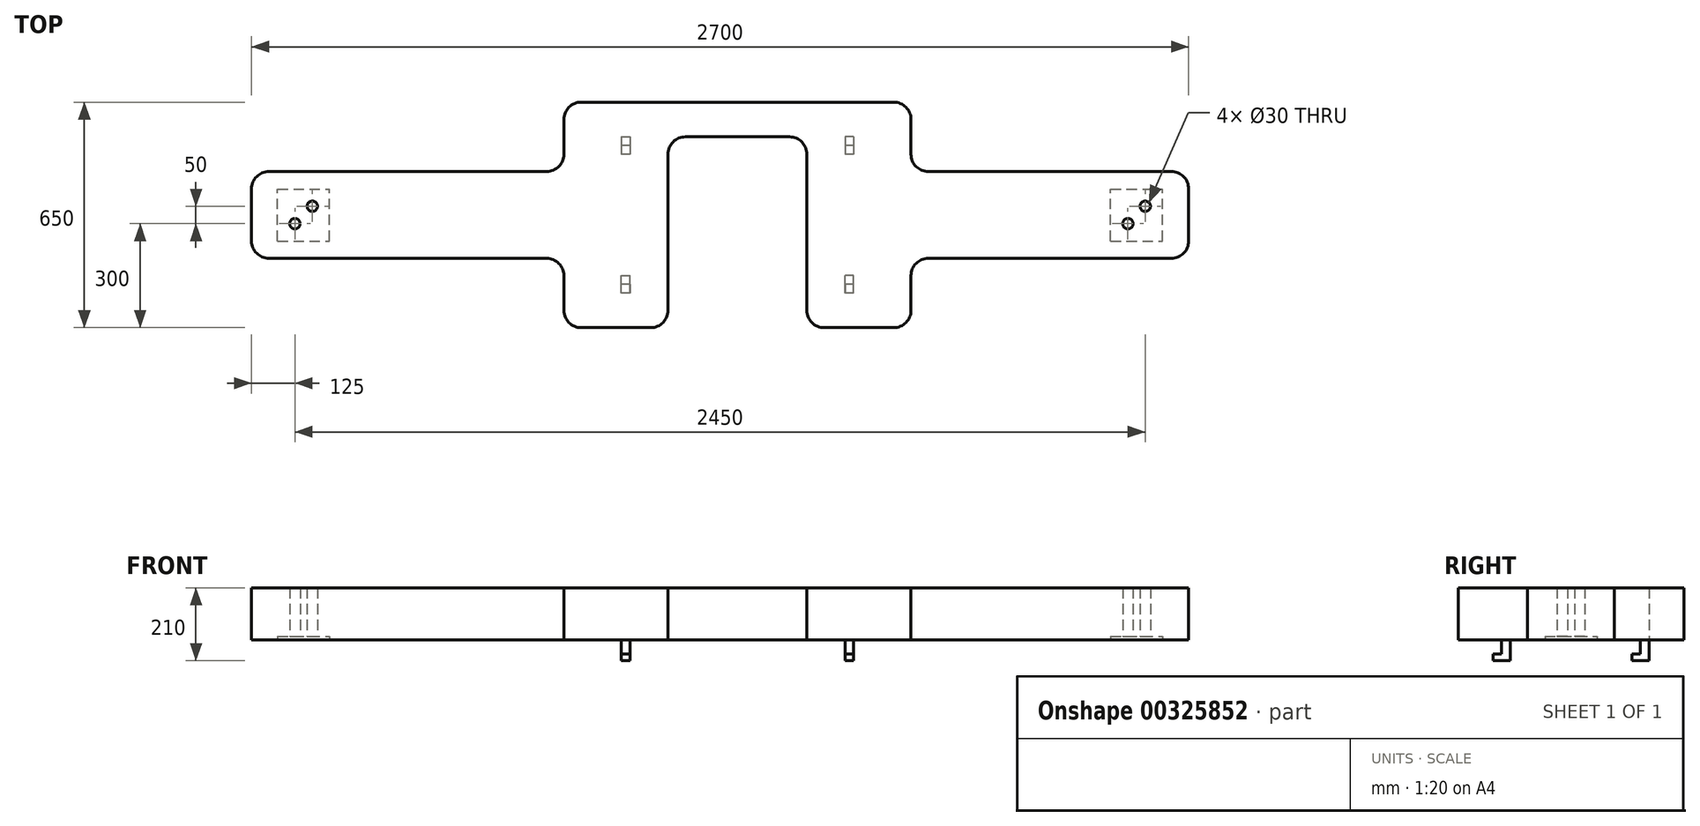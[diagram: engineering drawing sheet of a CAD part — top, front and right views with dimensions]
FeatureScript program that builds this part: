
annotation { "Feature Type Name" : "Feature", "Feature Type Description" : "" }
export const myFeature = defineFeature(function(context is Context, id is Id, definition is map)
    precondition{}
    {
        {
            var Q0;
            Q0=qCreatedBy(makeId("Top.planeOp"),FACE);
            var sketch = newSketch(context, id + "F0", { "sketchPlane" : qUnion([Q0])});
            skLineSegment(sketch, "E0", {"start": v(0, 0) * mm, "end": v(0, 250) * mm});
            skLineSegment(sketch, "E1", {"start": v(0, 250) * mm, "end": v(900, 250) * mm});
            skLineSegment(sketch, "E2.left", {"start": v(2700, 0) * mm, "end": v(2700, 250) * mm});
            skLineSegment(sketch, "E3", {"start": v(900, 250) * mm, "end": v(900, 450) * mm});
            skLineSegment(sketch, "E4", {"start": v(900, 450) * mm, "end": v(1900, 450) * mm});
            skLineSegment(sketch, "E5", {"start": v(1900, 450) * mm, "end": v(1900, 250) * mm});
            skLineSegment(sketch, "E6", {"start": v(1900, 0) * mm, "end": v(1900, -200) * mm});
            skLineSegment(sketch, "E7", {"start": v(1900, -200) * mm, "end": v(1600, -200) * mm});
            skLineSegment(sketch, "E8", {"start": v(1600, -200) * mm, "end": v(1600, 350) * mm});
            skLineSegment(sketch, "E9", {"start": v(1200, 350) * mm, "end": v(1600, 350) * mm});
            skLineSegment(sketch, "E10", {"start": v(2700, 250) * mm, "end": v(1900, 250) * mm});
            skLineSegment(sketch, "E11", {"start": v(2700, 0) * mm, "end": v(1900, 0) * mm});
            skLineSegment(sketch, "E12", {"start": v(0, 0) * mm, "end": v(900, 0) * mm});
            skLineSegment(sketch, "E13", {"start": v(900, 0) * mm, "end": v(900, -200) * mm});
            skLineSegment(sketch, "E14", {"start": v(900, -200) * mm, "end": v(1200, -200) * mm});
            skLineSegment(sketch, "E15", {"start": v(1200, -200) * mm, "end": v(1200, 350) * mm});
            skLineSegment(sketch, "E16", {"start": v(0, 125) * mm, "end": v(2700, 125) * mm, "construction": true});
            skSolve(sketch);
        }
        {
            var Q0;
            Q0 = qSketchRegion(id + "F0", true);
            extrude(context, id + "F1", {"entities" : qUnion([Q0]), "depth" : 150 * mm});
        }
        {
            var Q0;
            Q0=makeQuery(id+"F1.opExtrude","SWEPT_EDGE",EDGE,{"disambiguationData":[OSD([sQuery(id+"F0.wireOp",EDGE,"E8"),sQuery(id+"F0.wireOp",EDGE,"E9")])]});
            var Q1;
            Q1=makeQuery(id+"F1.opExtrude","SWEPT_EDGE",EDGE,{"disambiguationData":[OSD([sQuery(id+"F0.wireOp",EDGE,"CbPWlrPQ-xpmH-DLCr-Jztd-sM4HRHclp71n"),sQuery(id+"F0.wireOp",EDGE,"E9")])]});
            var Q2;
            Q2=makeQuery(id+"F1.opExtrude","SWEPT_EDGE",EDGE,{"disambiguationData":[OSD([sQuery(id+"F0.wireOp",EDGE,"VvWYzF3Y-HK12-tJQy-JKRe-ZAa0soEaOskw"),sQuery(id+"F0.wireOp",EDGE,"CbPWlrPQ-xpmH-DLCr-Jztd-sM4HRHclp71n")])]});
            var Q3;
            Q3=makeQuery(id+"F1.opExtrude","SWEPT_EDGE",EDGE,{"disambiguationData":[OSD([sQuery(id+"F0.wireOp",EDGE,"2RDTeN5u-19Zg-kb8m-eJnc-UEhqzuxQh641"),sQuery(id+"F0.wireOp",EDGE,"VvWYzF3Y-HK12-tJQy-JKRe-ZAa0soEaOskw")])]});
            var Q4;
            Q4=makeQuery(id+"F1.opExtrude","SWEPT_EDGE",EDGE,{"disambiguationData":[OSD([sQuery(id+"F0.wireOp",EDGE,"E7"),sQuery(id+"F0.wireOp",EDGE,"E8")])]});
            var Q5;
            Q5=makeQuery(id+"F1.opExtrude","SWEPT_EDGE",EDGE,{"disambiguationData":[OSD([sQuery(id+"F0.wireOp",EDGE,"E6"),sQuery(id+"F0.wireOp",EDGE,"E7")])]});
            var Q6;
            Q6=makeQuery(id+"F1.opExtrude","SWEPT_EDGE",EDGE,{"disambiguationData":[OSD([sQuery(id+"F0.wireOp",EDGE,"E2.bottom"),sQuery(id+"F0.wireOp",EDGE,"E6")])]});
            var Q7;
            Q7=makeQuery(id+"F1.opExtrude","SWEPT_EDGE",EDGE,{"disambiguationData":[OSD([sQuery(id+"F0.wireOp",EDGE,"E2.top"),sQuery(id+"F0.wireOp",EDGE,"E5")])]});
            var Q8;
            Q8=makeQuery(id+"F1.opExtrude","SWEPT_EDGE",EDGE,{"disambiguationData":[OSD([sQuery(id+"F0.wireOp",EDGE,"E4"),sQuery(id+"F0.wireOp",EDGE,"E5")])]});
            var Q9;
            Q9=makeQuery(id+"F1.opExtrude","SWEPT_EDGE",EDGE,{"disambiguationData":[OSD([sQuery(id+"F0.wireOp",EDGE,"E2.top"),sQuery(id+"F0.wireOp",EDGE,"E2.left")])]});
            var Q10;
            Q10=makeQuery(id+"F1.opExtrude","SWEPT_EDGE",EDGE,{"disambiguationData":[OSD([sQuery(id+"F0.wireOp",EDGE,"E2.bottom"),sQuery(id+"F0.wireOp",EDGE,"E2.left")])]});
            var Q11;
            Q11=makeQuery(id+"F1.opExtrude","SWEPT_EDGE",EDGE,{"disambiguationData":[OSD([sQuery(id+"F0.wireOp",EDGE,"E3"),sQuery(id+"F0.wireOp",EDGE,"E4")])]});
            var Q12;
            Q12=makeQuery(id+"F1.opExtrude","SWEPT_EDGE",EDGE,{"disambiguationData":[OSD([sQuery(id+"F0.wireOp",EDGE,"E1"),sQuery(id+"F0.wireOp",EDGE,"E3")])]});
            var Q13;
            Q13=makeQuery(id+"F1.opExtrude","SWEPT_EDGE",EDGE,{"disambiguationData":[OSD([sQuery(id+"F0.wireOp",EDGE,"E0"),sQuery(id+"F0.wireOp",EDGE,"E1")])]});
            var Q14;
            Q14=makeQuery(id+"F1.opExtrude","SWEPT_EDGE",EDGE,{"disambiguationData":[OSD([sQuery(id+"F0.wireOp",EDGE,"E0"),sQuery(id+"F0.wireOp",EDGE,"RZtDIs5I-CLOF-AWdb-lgDT-qq9BP0aAqrrl")])]});
            var Q15;
            Q15=makeQuery(id+"F1.opExtrude","SWEPT_EDGE",EDGE,{"disambiguationData":[OSD([sQuery(id+"F0.wireOp",EDGE,"RZtDIs5I-CLOF-AWdb-lgDT-qq9BP0aAqrrl"),sQuery(id+"F0.wireOp",EDGE,"2RDTeN5u-19Zg-kb8m-eJnc-UEhqzuxQh641")])]});
            fillet(context, id + "F2", {"entities" : qUnion([Q0, Q1, Q2, Q3, Q4, Q5, Q6, Q7, Q8, Q9, Q10, Q11, Q12, Q13, Q14, Q15]), "radius" : 50 * mm, "tangentPropagation" : true, "allowEdgeOverflow" : false});
        }
        {
            var Q0;
            Q0=makeQuery(id+"F1.opExtrude","CAP_FACE",FACE,{"disambiguationData":[OSD([sQuery(id+"F0.wireOp",EDGE,"E0"),sQuery(id+"F0.wireOp",EDGE,"E1"),sQuery(id+"F0.wireOp",EDGE,"RZtDIs5I-CLOF-AWdb-lgDT-qq9BP0aAqrrl"),sQuery(id+"F0.wireOp",EDGE,"E2.bottom"),sQuery(id+"F0.wireOp",EDGE,"E2.top"),sQuery(id+"F0.wireOp",EDGE,"E2.left"),sQuery(id+"F0.wireOp",EDGE,"E3"),sQuery(id+"F0.wireOp",EDGE,"E4"),sQuery(id+"F0.wireOp",EDGE,"E5"),sQuery(id+"F0.wireOp",EDGE,"E6"),sQuery(id+"F0.wireOp",EDGE,"E7"),sQuery(id+"F0.wireOp",EDGE,"E8"),sQuery(id+"F0.wireOp",EDGE,"2RDTeN5u-19Zg-kb8m-eJnc-UEhqzuxQh641"),sQuery(id+"F0.wireOp",EDGE,"VvWYzF3Y-HK12-tJQy-JKRe-ZAa0soEaOskw"),sQuery(id+"F0.wireOp",EDGE,"CbPWlrPQ-xpmH-DLCr-Jztd-sM4HRHclp71n"),sQuery(id+"F0.wireOp",EDGE,"E9")])],"isStart":true});
            var sketch = newSketch(context, id + "F3", { "sketchPlane" : qUnion([Q0])});
            skLineSegment(sketch, "E17.bottom", {"start": v(75, -50) * mm, "end": v(225, -50) * mm});
            skLineSegment(sketch, "E17.top", {"start": v(75, -200) * mm, "end": v(225, -200) * mm});
            skLineSegment(sketch, "E17.left", {"start": v(75, -50) * mm, "end": v(75, -200) * mm});
            skLineSegment(sketch, "E17.right", {"start": v(225, -50) * mm, "end": v(225, -200) * mm});
            skLineSegment(sketch, "E18.bottom", {"start": v(2475, -50) * mm, "end": v(2625, -50) * mm});
            skLineSegment(sketch, "E18.top", {"start": v(2475, -200) * mm, "end": v(2625, -200) * mm});
            skLineSegment(sketch, "E18.left", {"start": v(2475, -50) * mm, "end": v(2475, -200) * mm});
            skLineSegment(sketch, "E18.right", {"start": v(2625, -50) * mm, "end": v(2625, -200) * mm});
            skLineSegment(sketch, "E19", {"start": v(120, 0) * mm, "end": v(120, -50) * mm, "construction": true});
            skLineSegment(sketch, "E20", {"start": v(0, -125) * mm, "end": v(75, -125) * mm, "construction": true});
            skPoint(sketch, "E20.endSnap0", {"position": v(75, -125) * mm});
            skLineSegment(sketch, "E21", {"start": v(2625, -125) * mm, "end": v(2700, -125) * mm, "construction": true});
            skSolve(sketch);
        }
        {
            var Q0;
            Q0=makeQuery(id+"F3.imprint","IMPRINT",FACE,{"disambiguationData":[TD([[makeQuery(id+"F3.imprint","IMPRINT",EDGE,{"derivedFrom":sQuery(id+"F3.wireOp",EDGE,"E17.bottom")}),-1.0]])]});
            var Q1;
            Q1=makeQuery(id+"F3.imprint","IMPRINT",FACE,{"disambiguationData":[TD([[makeQuery(id+"F3.imprint","IMPRINT",EDGE,{"derivedFrom":sQuery(id+"F3.wireOp",EDGE,"E18.bottom")}),-1.0]])]});
            extrude(context, id + "F4", {"entities" : qUnion([Q0, Q1]), "operationType" : NewBodyOperationType.REMOVE, "oppositeDirection" : true, "depth" : 10 * mm});
        }
        {
            var Q0;
            Q0=makeQuery(id+"F1.opExtrude","SWEPT_EDGE",EDGE,{"disambiguationData":[OSD([sQuery(id+"F0.wireOp",EDGE,"E14"),sQuery(id+"F0.wireOp",EDGE,"E15")])]});
            var Q1;
            Q1=makeQuery(id+"F1.opExtrude","SWEPT_EDGE",EDGE,{"disambiguationData":[OSD([sQuery(id+"F0.wireOp",EDGE,"E13"),sQuery(id+"F0.wireOp",EDGE,"E14")])]});
            var Q2;
            Q2=makeQuery(id+"F1.opExtrude","SWEPT_EDGE",EDGE,{"disambiguationData":[OSD([sQuery(id+"F0.wireOp",EDGE,"E12"),sQuery(id+"F0.wireOp",EDGE,"E13")])]});
            fillet(context, id + "F5", {"entities" : qUnion([Q0, Q1, Q2]), "radius" : 50 * mm, "tangentPropagation" : true, "allowEdgeOverflow" : false});
        }
        {
            var Q0;
            Q0=makeQuery(id+"F4.boolean.opBoolean","COPY",FACE,{"derivedFrom":makeQuery(id+"F4.opExtrude","CAP_FACE",FACE,{"disambiguationData":[OSD([sQuery(id+"F3.wireOp",EDGE,"E17.bottom"),sQuery(id+"F3.wireOp",EDGE,"E17.top"),sQuery(id+"F3.wireOp",EDGE,"E17.left"),sQuery(id+"F3.wireOp",EDGE,"E17.right")])],"isStart":false})});
            var sketch = newSketch(context, id + "F6", { "sketchPlane" : qUnion([Q0])});
            skCircle(sketch, "E22", {"center": v(125, -100) * mm, "radius": 15 * mm});
            skCircle(sketch, "E23", {"center": v(175, -150) * mm, "radius": 15 * mm});
            skLineSegment(sketch, "E24", {"start": v(125, -100) * mm, "end": v(125, -50) * mm, "construction": true});
            skLineSegment(sketch, "E25", {"start": v(175, -150) * mm, "end": v(175, -200) * mm, "construction": true});
            skSolve(sketch);
        }
        {
            var Q0;
            Q0=makeQuery(id+"F6.imprint","IMPRINT",FACE,{"disambiguationData":[TD([[makeQuery(id+"F6.imprint","IMPRINT",EDGE,{"derivedFrom":sQuery(id+"F6.wireOp",EDGE,"E23")}),1.0]])]});
            var Q1;
            Q1=makeQuery(id+"F6.imprint","IMPRINT",FACE,{"disambiguationData":[TD([[makeQuery(id+"F6.imprint","IMPRINT",EDGE,{"derivedFrom":sQuery(id+"F6.wireOp",EDGE,"E22")}),1.0]])]});
            var Q2;
            Q2=sQuery(id+"F6.wireOp",EDGE,"E22");
            var Q3;
            Q3=sQuery(id+"F6.wireOp",EDGE,"E23");
            extrude(context, id + "F7", {"entities" : qUnion([Q0, Q1]), "operationType" : NewBodyOperationType.REMOVE, "surfaceEntities" : qUnion([Q2, Q3]), "oppositeDirection" : true, "depth" : 200 * mm});
        }
        {
            var Q0;
            Q0=makeQuery(id+"F4.boolean.opBoolean","COPY",FACE,{"derivedFrom":makeQuery(id+"F4.opExtrude","CAP_FACE",FACE,{"disambiguationData":[OSD([sQuery(id+"F3.wireOp",EDGE,"E18.bottom"),sQuery(id+"F3.wireOp",EDGE,"E18.top"),sQuery(id+"F3.wireOp",EDGE,"E18.left"),sQuery(id+"F3.wireOp",EDGE,"E18.right")])],"isStart":false})});
            var sketch = newSketch(context, id + "F8", { "sketchPlane" : qUnion([Q0])});
            skCircle(sketch, "E26", {"center": v(2525, -100) * mm, "radius": 15 * mm});
            skCircle(sketch, "E27", {"center": v(2575, -150) * mm, "radius": 15 * mm});
            skLineSegment(sketch, "E28", {"start": v(2525, -100) * mm, "end": v(2475, -100) * mm, "construction": true});
            skLineSegment(sketch, "E29", {"start": v(2575, -150) * mm, "end": v(2625, -150) * mm, "construction": true});
            skLineSegment(sketch, "E30", {"start": v(2525, -100) * mm, "end": v(2525, -50) * mm, "construction": true});
            skLineSegment(sketch, "E31", {"start": v(2575, -150) * mm, "end": v(2575, -200) * mm, "construction": true});
            skSolve(sketch);
        }
        {
            var Q0;
            Q0 = qSketchRegion(id + "F8", true);
            extrude(context, id + "F9", {"entities" : qUnion([Q0]), "operationType" : NewBodyOperationType.REMOVE, "oppositeDirection" : true, "depth" : 200 * mm});
        }
        {
            var Q0;
            Q0=makeQuery(id+"F1.opExtrude","CAP_FACE",FACE,{"disambiguationData":[OSD([sQuery(id+"F0.wireOp",EDGE,"E0"),sQuery(id+"F0.wireOp",EDGE,"E1"),sQuery(id+"F0.wireOp",EDGE,"E2.left"),sQuery(id+"F0.wireOp",EDGE,"E3"),sQuery(id+"F0.wireOp",EDGE,"E4"),sQuery(id+"F0.wireOp",EDGE,"E5"),sQuery(id+"F0.wireOp",EDGE,"E6"),sQuery(id+"F0.wireOp",EDGE,"E7"),sQuery(id+"F0.wireOp",EDGE,"E8"),sQuery(id+"F0.wireOp",EDGE,"E9"),sQuery(id+"F0.wireOp",EDGE,"E10"),sQuery(id+"F0.wireOp",EDGE,"E11"),sQuery(id+"F0.wireOp",EDGE,"E12"),sQuery(id+"F0.wireOp",EDGE,"E13"),sQuery(id+"F0.wireOp",EDGE,"E14"),sQuery(id+"F0.wireOp",EDGE,"E15")])],"isStart":true});
            var sketch = newSketch(context, id + "F10", { "sketchPlane" : qUnion([Q0])});
            skLineSegment(sketch, "E32.bottom", {"start": v(1065, 100) * mm, "end": v(1090, 100) * mm});
            skLineSegment(sketch, "E32.top", {"start": v(1065, 50) * mm, "end": v(1090, 50) * mm});
            skLineSegment(sketch, "E32.left", {"start": v(1065, 100) * mm, "end": v(1065, 50) * mm});
            skLineSegment(sketch, "E32.right", {"start": v(1090, 100) * mm, "end": v(1090, 50) * mm});
            skLineSegment(sketch, "E33.MirrorCS", {"start": v(1735, 100) * mm, "end": v(1710, 100) * mm});
            skLineSegment(sketch, "E34.MirrorCS", {"start": v(1735, 50) * mm, "end": v(1710, 50) * mm});
            skLineSegment(sketch, "E35.MirrorCS", {"start": v(1710, 100) * mm, "end": v(1710, 50) * mm});
            skLineSegment(sketch, "E36.MirrorCS", {"start": v(1735, 100) * mm, "end": v(1735, 50) * mm});
            skLineSegment(sketch, "E37.MirrorCS", {"start": v(1065, -300) * mm, "end": v(1090, -300) * mm});
            skLineSegment(sketch, "E38.MirrorCS", {"start": v(1065, -350) * mm, "end": v(1090, -350) * mm});
            skLineSegment(sketch, "E39.MirrorCS", {"start": v(1735, -300) * mm, "end": v(1710, -300) * mm});
            skLineSegment(sketch, "E40.MirrorCS", {"start": v(1735, -350) * mm, "end": v(1710, -350) * mm});
            skLineSegment(sketch, "E41.MirrorCS", {"start": v(1065, -350) * mm, "end": v(1065, -300) * mm});
            skLineSegment(sketch, "E42.MirrorCS", {"start": v(1735, -350) * mm, "end": v(1735, -300) * mm});
            skLineSegment(sketch, "E43.MirrorCS", {"start": v(1710, -350) * mm, "end": v(1710, -300) * mm});
            skLineSegment(sketch, "E44.MirrorCS", {"start": v(1090, -350) * mm, "end": v(1090, -300) * mm});
            skSolve(sketch);
        }
        {
            var Q0;
            Q0 = qSketchRegion(id + "F10", true);
            extrude(context, id + "F11", {"entities" : qUnion([Q0]), "operationType" : NewBodyOperationType.ADD, "depth" : 60 * mm});
        }
        {
            var Q0;
            Q0=makeQuery(id+"F11.opExtrude","SWEPT_FACE",FACE,{"disambiguationData":[OSD([sQuery(id+"F10.wireOp",EDGE,"E32.left")])]});
            var sketch = newSketch(context, id + "F12", { "sketchPlane" : qUnion([Q0])});
            skLineSegment(sketch, "E45", {"start": v(100, -40) * mm, "end": v(75, -40) * mm});
            skLineSegment(sketch, "E46", {"start": v(75, -40) * mm, "end": v(75, 0) * mm});
            skLineSegment(sketch, "E47", {"start": v(75, 0) * mm, "end": v(100, 0) * mm});
            skLineSegment(sketch, "E48", {"start": v(100, 0) * mm, "end": v(100, -40) * mm});
            skSolve(sketch);
        }
        {
            var Q0;
            Q0=makeQuery(id+"F12.imprint","IMPRINT",FACE,{"disambiguationData":[TD([[makeQuery(id+"F12.imprint","IMPRINT",EDGE,{"derivedFrom":sQuery(id+"F12.wireOp",EDGE,"E45")}),-1.0]])]});
            extrude(context, id + "F13", {"entities" : qUnion([Q0]), "operationType" : NewBodyOperationType.REMOVE, "oppositeDirection" : true, "depth" : 100 * mm});
        }
        {
            var Q0;
            Q0=makeQuery(id+"F11.opExtrude","SWEPT_FACE",FACE,{"disambiguationData":[OSD([sQuery(id+"F10.wireOp",EDGE,"E35.MirrorCS")])]});
            var sketch = newSketch(context, id + "F14", { "sketchPlane" : qUnion([Q0])});
            skLineSegment(sketch, "E49", {"start": v(100, 0) * mm, "end": v(75, 0) * mm});
            skLineSegment(sketch, "E50", {"start": v(75, 0) * mm, "end": v(75, -40) * mm});
            skLineSegment(sketch, "E51", {"start": v(75, -40) * mm, "end": v(100, -40) * mm});
            skLineSegment(sketch, "E52", {"start": v(100, -40) * mm, "end": v(100, 0) * mm});
            skSolve(sketch);
        }
        {
            var Q0;
            Q0=makeQuery(id+"F14.imprint","IMPRINT",FACE,{"disambiguationData":[TD([[makeQuery(id+"F14.imprint","IMPRINT",EDGE,{"derivedFrom":sQuery(id+"F14.wireOp",EDGE,"E49")}),1.0]])]});
            extrude(context, id + "F15", {"entities" : qUnion([Q0]), "operationType" : NewBodyOperationType.REMOVE, "oppositeDirection" : true, "depth" : 100 * mm});
        }
        {
            var Q0;
            Q0=makeQuery(id+"F11.opExtrude","SWEPT_FACE",FACE,{"disambiguationData":[OSD([sQuery(id+"F10.wireOp",EDGE,"E41.MirrorCS")])]});
            var sketch = newSketch(context, id + "F16", { "sketchPlane" : qUnion([Q0])});
            skLineSegment(sketch, "E53", {"start": v(-300, 0) * mm, "end": v(-325, 0) * mm});
            skLineSegment(sketch, "E54", {"start": v(-325, 0) * mm, "end": v(-325, -40) * mm});
            skLineSegment(sketch, "E55", {"start": v(-325, -40) * mm, "end": v(-300, -40) * mm});
            skLineSegment(sketch, "E56", {"start": v(-300, -40) * mm, "end": v(-300, 0) * mm});
            skSolve(sketch);
        }
        {
            var Q0;
            Q0=makeQuery(id+"F16.imprint","IMPRINT",FACE,{"disambiguationData":[TD([[makeQuery(id+"F16.imprint","IMPRINT",EDGE,{"derivedFrom":sQuery(id+"F16.wireOp",EDGE,"E53")}),-1.0]])]});
            extrude(context, id + "F17", {"entities" : qUnion([Q0]), "operationType" : NewBodyOperationType.REMOVE, "oppositeDirection" : true, "depth" : 1000 * mm});
        }
    });
